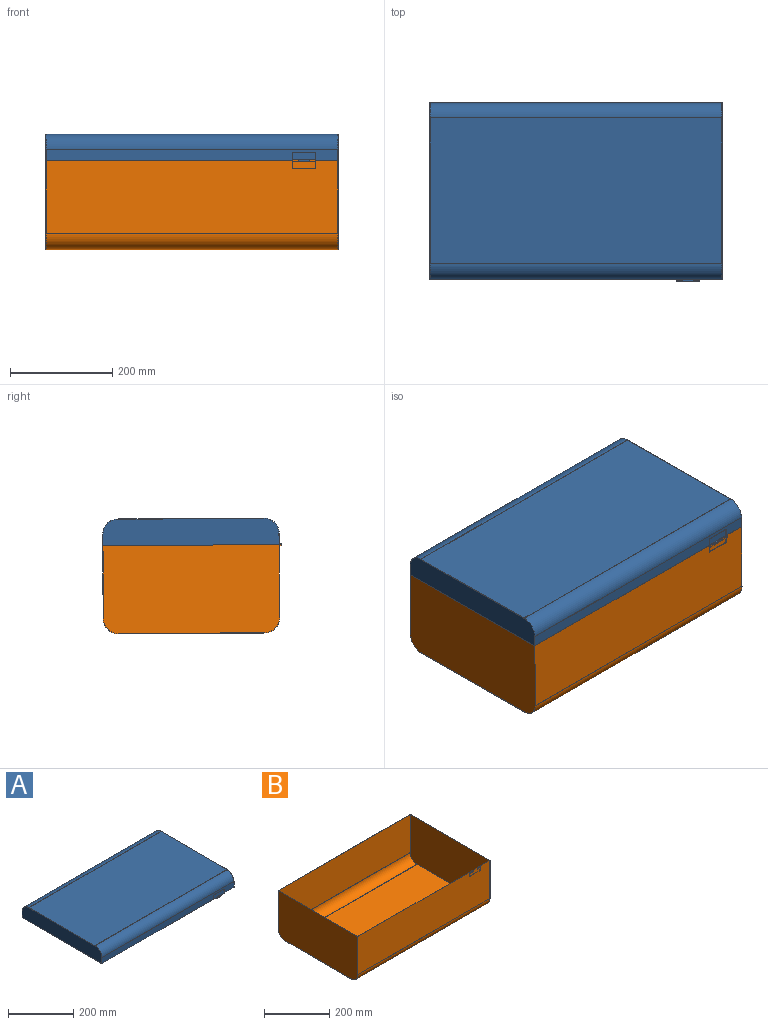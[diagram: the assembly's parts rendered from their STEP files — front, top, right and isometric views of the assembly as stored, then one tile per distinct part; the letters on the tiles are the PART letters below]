
ASSEMBLY  parts=2 mates=1
PART A: 36 faces, bbox 573x350x54 mm
  f0: plane 573x347mm, normal (0,0,-1), area 909.5mm2, adj f1,f2,f6,f7,f8,f10,f11,f16
  f1: plane 573x22mm, normal (0,-1,0), area 11885.3mm2, adj f0,f5,f6,f7,f8,f9,f10
  f2: plane 573x22mm, normal (0,1,0), area 12606mm2, adj f0,f3,f6,f7
  f3: cylinder r=30mm len=573mm, axis (-1,0,0), area 27002mm2, adj f2,f4,f6,f7
  f4: plane 573x286mm, normal (0,0,1), area 163878mm2, adj f3,f5,f6,f7
  f5: cylinder r=30mm len=573mm, axis (-1,0,0), area 27002mm2, adj f1,f4,f6,f7
  f6: plane 346x52mm, normal (1,0,0), area 17605.7mm2, adj f0,f1,f2,f3,f4,f5
  f7: plane 346x52mm, normal (-1,0,0), area 17605.7mm2, adj f0,f1,f2,f3,f4,f5
  f8: plane 15.5x1mm, normal (1,0,0), area 15.5mm2, adj f0,f1,f9,f11
  f9: plane 46.5x1mm, normal (0,0,1), area 46.5mm2, adj f1,f8,f10,f11
  f10: plane 15.5x1mm, normal (-1,0,0), area 15.5mm2, adj f0,f1,f9,f11
  f11: plane 46.5x15.5mm, normal (0,-1,0), area 680.9mm2, adj f0,f8,f9,f10,f12,f13,f14
  f12: plane 4x3mm, normal (-1,0,0), area 12mm2, adj f11,f14,f15,f16,f17
  f13: plane 4x3mm, normal (1,0,0), area 12mm2, adj f11,f14,f15,f16,f17
  f14: plane 19.9x3mm, normal (0,0,1), area 59.7mm2, adj f11,f12,f13,f15
  f15: plane 19.9x4mm, normal (0,-1,0), area 79.6mm2, adj f12,f13,f14,f17
  f16: plane 19.9x2mm, normal (0,1,0), area 39.8mm2, adj f0,f12,f13,f17,f18
  f17: plane 19.9x3mm, normal (0,0,-1), area 59.7mm2, adj f12,f13,f15,f16
  f18: plane 18.9x0.5mm, normal (0,0,1), area 9.4mm2, adj f16,f30,f31,f34
  f19: plane 572x22mm, normal (0,1,0), area 11901.5mm2, adj f0,f23,f24,f25,f26,f27,f28
  f20: plane 572x22mm, normal (0,-1,0), area 12584mm2, adj f0,f21,f24,f25
  f21: cylinder r=29.5mm len=572mm, axis (-1,0,0), area 26505.6mm2, adj f20,f22,f24,f25
  f22: plane 572x286mm, normal (0,0,-1), area 163592mm2, adj f21,f23,f24,f25
  f23: cylinder r=29.5mm len=572mm, axis (-1,0,0), area 26505.6mm2, adj f19,f22,f24,f25
  f24: plane 345x51.5mm, normal (-1,0,0), area 17394mm2, adj f0,f19,f20,f21,f22,f23
  f25: plane 345x51.5mm, normal (1,0,0), area 17394mm2, adj f0,f19,f20,f21,f22,f23
  f26: plane 15x1mm, normal (-1,0,0), area 15mm2, adj f0,f19,f27,f29
  f27: plane 45.5x1mm, normal (0,0,-1), area 45.5mm2, adj f19,f26,f28,f29
  f28: plane 15x1mm, normal (1,0,0), area 15mm2, adj f0,f19,f27,f29
  f29: plane 45.5x15mm, normal (0,1,0), area 654.1mm2, adj f0,f26,f27,f28,f30,f31,f32
  f30: plane 3x3mm, normal (1,0,0), area 7.5mm2, adj f0,f18,f29,f32,f33,f34,f35
  f31: plane 3x3mm, normal (-1,0,0), area 7.5mm2, adj f0,f18,f29,f32,f33,f34,f35
  f32: plane 18.9x3mm, normal (0,0,-1), area 56.7mm2, adj f29,f30,f31,f33
  f33: plane 18.9x3mm, normal (0,1,0), area 56.7mm2, adj f30,f31,f32,f35
  f34: plane 18.9x1.5mm, normal (0,-1,0), area 28.3mm2, adj f18,f30,f31,f35
  f35: plane 18.9x2mm, normal (0,0,1), area 37.8mm2, adj f30,f31,f33,f34
PART B: 46 faces, bbox 573x350x175 mm
  f0: plane 573x347mm, normal (0,0,1), area 896.2mm2, adj f2,f6,f7,f8,f9,f10,f19,f21
  f1: plane 20.9x0.5mm, normal (0,0,1), area 10.4mm2, adj f12,f19,f21,f35,f36,f40
  f2: plane 573x143mm, normal (0,-1,0), area 81218.3mm2, adj f0,f3,f7,f8,f9,f10,f11
  f3: cylinder r=30mm len=573mm, axis (-1,0,0), area 27002mm2, adj f2,f4,f7,f8
  f4: plane 573x286mm, normal (0,0,-1), area 163878mm2, adj f3,f5,f7,f8
  f5: cylinder r=30mm len=573mm, axis (-1,0,0), area 27002mm2, adj f4,f6,f7,f8
  f6: plane 573x143mm, normal (0,1,0), area 81939mm2, adj f0,f5,f7,f8
  f7: plane 346x173mm, normal (1,0,0), area 59471.7mm2, adj f0,f2,f3,f4,f5,f6
  f8: plane 346x173mm, normal (-1,0,0), area 59471.7mm2, adj f0,f2,f3,f4,f5,f6
  f9: plane 17.5x4mm, normal (1,0,0), area 27.5mm2, adj f0,f2,f11,f12,f14,f15,f21,f22
  f10: plane 17.5x4mm, normal (-1,0,0), area 27.5mm2, adj f0,f2,f11,f12,f16,f18,f19,f20
  f11: plane 46.5x1mm, normal (0,0,-1), area 46.5mm2, adj f2,f9,f10,f12
  f12: plane 46.5x15.5mm, normal (0,-1,0), area 667.6mm2, adj f1,f9,f10,f11,f13,f14,f16,f17
  f13: plane 4x3mm, normal (-1,0,0), area 12mm2, adj f12,f14,f15,f21,f22
  f14: plane 13.3x3mm, normal (0,0,-1), area 39.9mm2, adj f9,f12,f13,f15
  f15: plane 13.3x4mm, normal (0,-1,0), area 53.2mm2, adj f9,f13,f14,f22
  f16: plane 13.3x3mm, normal (0,0,-1), area 39.9mm2, adj f10,f12,f17,f18
  f17: plane 4x3mm, normal (1,0,0), area 12mm2, adj f12,f16,f18,f19,f20
  f18: plane 13.3x4mm, normal (0,-1,0), area 53.2mm2, adj f10,f16,f17,f20
  f19: plane 13.3x2mm, normal (0,1,0), area 26.6mm2, adj f0,f1,f10,f17,f20,f23
  f20: plane 13.3x3mm, normal (0,0,1), area 39.9mm2, adj f10,f17,f18,f19
  f21: plane 13.3x2mm, normal (0,1,0), area 26.6mm2, adj f0,f1,f9,f13,f22,f24
  f22: plane 13.3x3mm, normal (0,0,1), area 39.9mm2, adj f9,f13,f15,f21
  f23: plane 12.3x0.5mm, normal (0,0,-1), area 6.2mm2, adj f19,f33,f40,f42
  f24: plane 12.3x0.5mm, normal (0,0,-1), area 6.1mm2, adj f21,f32,f36,f44
  f25: plane 572x143mm, normal (0,1,0), area 81113.5mm2, adj f0,f26,f30,f31,f32,f33,f34
  f26: cylinder r=29.5mm len=572mm, axis (-1,0,0), area 26505.6mm2, adj f25,f27,f30,f31
  f27: plane 572x286mm, normal (0,0,1), area 163592mm2, adj f26,f28,f30,f31
  f28: cylinder r=29.5mm len=572mm, axis (-1,0,0), area 26505.6mm2, adj f27,f29,f30,f31
  f29: plane 572x143mm, normal (0,-1,0), area 81796mm2, adj f0,f28,f30,f31
  f30: plane 345x172.5mm, normal (-1,0,0), area 59139mm2, adj f0,f25,f26,f27,f28,f29
  f31: plane 345x172.5mm, normal (1,0,0), area 59139mm2, adj f0,f25,f26,f27,f28,f29
  f32: plane 16.5x4mm, normal (-1,0,0), area 22.5mm2, adj f0,f24,f25,f34,f35,f37,f38,f44
  f33: plane 16.5x4mm, normal (1,0,0), area 22.5mm2, adj f0,f23,f25,f34,f35,f39,f41,f42
  f34: plane 45.5x1mm, normal (0,0,1), area 45.5mm2, adj f25,f32,f33,f35
  f35: plane 45.5x15mm, normal (0,1,0), area 645.6mm2, adj f1,f32,f33,f34,f36,f37,f39,f40
  f36: plane 3x3mm, normal (1,0,0), area 7.5mm2, adj f1,f24,f35,f37,f38,f44,f45
  f37: plane 12.3x3mm, normal (0,0,1), area 36.9mm2, adj f32,f35,f36,f38
  f38: plane 12.3x3mm, normal (0,1,0), area 36.9mm2, adj f32,f36,f37,f45
  f39: plane 12.3x3mm, normal (0,0,1), area 36.9mm2, adj f33,f35,f40,f41
  f40: plane 3x3mm, normal (-1,0,0), area 7.5mm2, adj f1,f23,f35,f39,f41,f42,f43
  f41: plane 12.3x3mm, normal (0,1,0), area 36.9mm2, adj f33,f39,f40,f43
  f42: plane 12.3x1.5mm, normal (0,-1,0), area 18.5mm2, adj f23,f33,f40,f43
  f43: plane 12.3x2mm, normal (0,0,-1), area 24.6mm2, adj f33,f40,f41,f42
  f44: plane 12.3x1.5mm, normal (0,-1,0), area 18.4mm2, adj f24,f32,f36,f45
  f45: plane 12.3x2mm, normal (0,0,-1), area 24.6mm2, adj f32,f36,f38,f44
PLACE A rot(axis=(-1,0,0),0.3deg) t=(23.04,5.73,8.9)mm
PLACE B rot(axis=(-1,0,0),0.3deg) t=(23.04,5.73,8.9)mm
MATE revolute A.f12 <-> B.f17  axis (1,0,0) through (519.01,-169.27,96.41)mm
